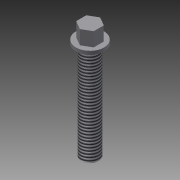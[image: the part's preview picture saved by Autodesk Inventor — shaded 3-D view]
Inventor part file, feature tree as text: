
AUTODESK INVENTOR PART (.ipt)
format: ipt  version: 2015 (Build 190159000, 159)  size: 97,792 bytes
history: native  units: mm
features: extrude x3, sketch x3, thread x1, chamfer x1
ambient origin geometry x8: Origin, YZ Plane, XZ Plane, XY Plane, X Axis, Y Axis, Z Axis, Center Point
bodies: 实体1 (feature_tree)
feature tree (8):
  extrude  "拉伸1"  Depth=1.0mm TaperAngle=0.0deg
  extrude  "拉伸2"  Depth=4.0mm TaperAngle=0.0deg
  extrude  "拉伸3"  Depth=28.0mm TaperAngle=0.0deg
  thread  "螺纹1"  [1 undecoded]
  chamfer  "倒角1"  Distance=0.25mm Angle=45.0deg
  sketch  "草图1"  dims[d0=8.0mm d1=1.0mm d2=0.0mm]
  sketch  "草图2"  dims[d3=5.0mm d4=4.0mm d5=0.0mm]
  sketch  "草图3"  dims[d6=5.0mm d7=28.0mm d8=0.0mm d9=10.0mm d10=0.0mm d11=0.25mm d12=2.0mm d13=45.0deg]
note: 1 required parameter value undecoded (feature->parameter linkage not recoverable at this tier; creation-order binding heuristic only, values carry confidence <= 0.55)
